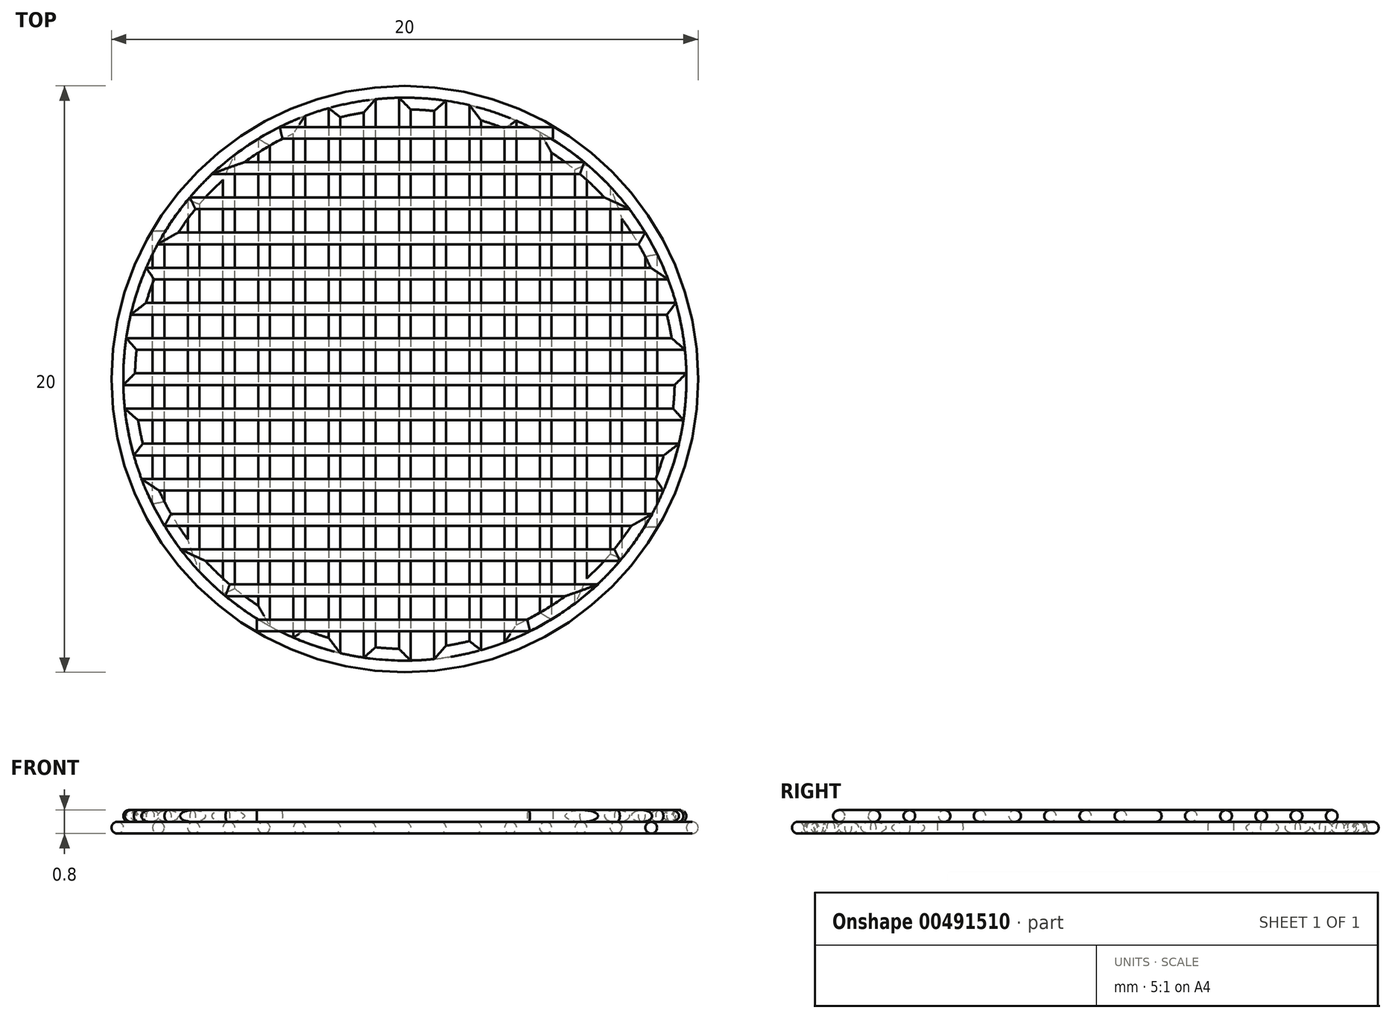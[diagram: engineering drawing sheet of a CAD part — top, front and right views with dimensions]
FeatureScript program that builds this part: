
annotation { "Feature Type Name" : "Feature", "Feature Type Description" : "" }
export const myFeature = defineFeature(function(context is Context, id is Id, definition is map)
    precondition{}
    {
        {
            assignVariable(context, id + "F0", {"name" : "d", "anyValue" : 0.4 * mm});
        }
        {
            var Q0;
            Q0=qCreatedBy(makeId("Top.planeOp"),FACE);
            cPlane(context, id + "F1", {"entities" : qUnion([Q0]), "cplaneType" : CPlaneType.OFFSET, "offset" : getVariable(context, 'd') / 2, "width" : 150 * mm, "height" : 150 * mm});
        }
        {
            var Q0;
            Q0=qCreatedBy(id+"F1.planeOp",FACE);
            var sketch = newSketch(context, id + "F2", { "sketchPlane" : qUnion([Q0])});
            skLineSegment(sketch, "E0.bottom", {"start": v(10, 10) * mm, "end": v(-10, 10) * mm, "construction": true});
            skLineSegment(sketch, "E0.top", {"start": v(10, -10) * mm, "end": v(-10, -10) * mm, "construction": true});
            skLineSegment(sketch, "E0.left", {"start": v(10, 10) * mm, "end": v(10, -10) * mm, "construction": true});
            skLineSegment(sketch, "E0.right", {"start": v(-10, 10) * mm, "end": v(-10, -10) * mm, "construction": true});
            skPoint(sketch, "E0.middle", {"position": v(0, 0) * mm});
            skCircle(sketch, "E1", {"center": v(0, 0) * mm, "radius": 9.8 * mm});
            skCircle(sketch, "E2", {"center": v(0, 0) * mm, "radius": 9.4 * mm, "construction": true});
            skLineSegment(sketch, "E3", {"start": v(10, -10) * mm, "end": v(9.6, -10) * mm, "construction": true});
            skLineSegment(sketch, "E4", {"start": v(9.6, -10) * mm, "end": v(8.4, -10) * mm, "construction": true});
            skLineSegment(sketch, "E5", {"start": v(8.4, -10) * mm, "end": v(7.2, -10) * mm, "construction": true});
            skLineSegment(sketch, "E6", {"start": v(7.2, -10) * mm, "end": v(6, -10) * mm, "construction": true});
            skLineSegment(sketch, "E7", {"start": v(6, -10) * mm, "end": v(4.8, -10) * mm, "construction": true});
            skLineSegment(sketch, "E8", {"start": v(4.8, -10) * mm, "end": v(3.6, -10) * mm, "construction": true});
            skLineSegment(sketch, "E9", {"start": v(3.6, -10) * mm, "end": v(2.4, -10) * mm, "construction": true});
            skLineSegment(sketch, "E10", {"start": v(2.4, -10) * mm, "end": v(1.2, -10) * mm, "construction": true});
            skLineSegment(sketch, "E11", {"start": v(1.2, -10) * mm, "end": v(0, -10) * mm, "construction": true});
            skLineSegment(sketch, "E12", {"start": v(0, -10) * mm, "end": v(-1.2, -10) * mm, "construction": true});
            skLineSegment(sketch, "E13", {"start": v(-1.2, -10) * mm, "end": v(-2.4, -10) * mm, "construction": true});
            skLineSegment(sketch, "E14", {"start": v(-2.4, -10) * mm, "end": v(-3.6, -10) * mm, "construction": true});
            skLineSegment(sketch, "E15", {"start": v(-3.6, -10) * mm, "end": v(-4.8, -10) * mm, "construction": true});
            skLineSegment(sketch, "E16", {"start": v(-4.8, -10) * mm, "end": v(-6, -10) * mm, "construction": true});
            skLineSegment(sketch, "E17", {"start": v(-6, -10) * mm, "end": v(-10, -10) * mm, "construction": true});
            skLineSegment(sketch, "E18", {"start": v(-6, -10) * mm, "end": v(-7.2, -10) * mm, "construction": true});
            skLineSegment(sketch, "E19", {"start": v(-7.2, -10) * mm, "end": v(-8.4, -10) * mm, "construction": true});
            skLineSegment(sketch, "E20", {"start": v(-8.4, -10) * mm, "end": v(-9.6, -10) * mm, "construction": true});
            skLineSegment(sketch, "E21", {"start": v(-9.6, -10) * mm, "end": v(-10, -10) * mm, "construction": true});
            skLineSegment(sketch, "E22", {"start": v(9.6, -10) * mm, "end": v(9.6, 10) * mm, "construction": true});
            skLineSegment(sketch, "E23", {"start": v(9.6, 10) * mm, "end": v(10, 10) * mm, "construction": true});
            skLineSegment(sketch, "E24", {"start": v(-9.6, -10) * mm, "end": v(-9.6, 10) * mm, "construction": true});
            skLineSegment(sketch, "E25", {"start": v(-9.6, 10) * mm, "end": v(-10, 10) * mm, "construction": true});
            skLineSegment(sketch, "E26", {"start": v(7.2, -10) * mm, "end": v(7.2, -6.04) * mm, "construction": true});
            skLineSegment(sketch, "E27", {"start": v(7.2, -6.04) * mm, "end": v(7.2, 6.04) * mm});
            skLineSegment(sketch, "E28", {"start": v(7.2, 6.04) * mm, "end": v(7.2, 10) * mm, "construction": true});
            skLineSegment(sketch, "E29", {"start": v(6, -10) * mm, "end": v(6, -7.24) * mm, "construction": true});
            skLineSegment(sketch, "E30", {"start": v(6, -7.24) * mm, "end": v(6, 7.24) * mm});
            skLineSegment(sketch, "E31", {"start": v(6, 7.24) * mm, "end": v(6, 10) * mm, "construction": true});
            skLineSegment(sketch, "E32", {"start": v(6, 10) * mm, "end": v(7.2, 10) * mm, "construction": true});
            skLineSegment(sketch, "E33", {"start": v(4.8, -10) * mm, "end": v(4.8, -8.08) * mm, "construction": true});
            skLineSegment(sketch, "E34", {"start": v(4.8, -8.08) * mm, "end": v(4.8, 8.08) * mm});
            skLineSegment(sketch, "E35", {"start": v(4.8, 8.08) * mm, "end": v(4.8, 10) * mm, "construction": true});
            skLineSegment(sketch, "E36", {"start": v(4.8, 10) * mm, "end": v(6, 10) * mm, "construction": true});
            skLineSegment(sketch, "E37", {"start": v(3.6, -10) * mm, "end": v(3.6, -8.68) * mm, "construction": true});
            skLineSegment(sketch, "E38", {"start": v(3.6, -8.68) * mm, "end": v(3.6, 8.68) * mm});
            skLineSegment(sketch, "E39", {"start": v(3.6, 8.68) * mm, "end": v(3.6, 10) * mm, "construction": true});
            skLineSegment(sketch, "E40", {"start": v(3.6, 10) * mm, "end": v(4.8, 10) * mm, "construction": true});
            skLineSegment(sketch, "E41", {"start": v(2.4, -10) * mm, "end": v(2.4, -9.09) * mm, "construction": true});
            skLineSegment(sketch, "E42", {"start": v(2.4, -9.09) * mm, "end": v(2.4, 9.09) * mm});
            skLineSegment(sketch, "E43", {"start": v(2.4, 9.09) * mm, "end": v(2.4, 10) * mm, "construction": true});
            skLineSegment(sketch, "E44", {"start": v(2.4, 10) * mm, "end": v(3.6, 10) * mm, "construction": true});
            skLineSegment(sketch, "E45", {"start": v(1.2, -10) * mm, "end": v(1.2, -9.32) * mm, "construction": true});
            skLineSegment(sketch, "E46", {"start": v(1.2, -9.32) * mm, "end": v(1.2, 9.32) * mm});
            skLineSegment(sketch, "E47", {"start": v(1.2, 9.32) * mm, "end": v(1.2, 10) * mm, "construction": true});
            skLineSegment(sketch, "E48", {"start": v(1.2, 10) * mm, "end": v(2.4, 10) * mm, "construction": true});
            skLineSegment(sketch, "E49", {"start": v(0, -10) * mm, "end": v(0, -9.4) * mm, "construction": true});
            skLineSegment(sketch, "E50", {"start": v(0, -9.4) * mm, "end": v(0, 9.4) * mm});
            skLineSegment(sketch, "E51", {"start": v(0, 9.4) * mm, "end": v(0, 10) * mm, "construction": true});
            skLineSegment(sketch, "E52", {"start": v(0, 10) * mm, "end": v(1.2, 10) * mm, "construction": true});
            skLineSegment(sketch, "E53", {"start": v(-1.2, -10) * mm, "end": v(-1.2, -9.32) * mm, "construction": true});
            skLineSegment(sketch, "E54", {"start": v(-1.2, -9.32) * mm, "end": v(-1.2, 9.32) * mm});
            skLineSegment(sketch, "E55", {"start": v(-1.2, 9.32) * mm, "end": v(-1.2, 10) * mm, "construction": true});
            skLineSegment(sketch, "E56", {"start": v(-1.2, 10) * mm, "end": v(0, 10) * mm, "construction": true});
            skLineSegment(sketch, "E57", {"start": v(-2.4, -10) * mm, "end": v(-2.4, -9.09) * mm, "construction": true});
            skLineSegment(sketch, "E58", {"start": v(-2.4, -9.09) * mm, "end": v(-2.4, 9.09) * mm});
            skLineSegment(sketch, "E59", {"start": v(-2.4, 9.09) * mm, "end": v(-2.4, 10) * mm, "construction": true});
            skLineSegment(sketch, "E60", {"start": v(-2.4, 10) * mm, "end": v(-1.2, 10) * mm, "construction": true});
            skLineSegment(sketch, "E61", {"start": v(-3.6, -10) * mm, "end": v(-3.6, -8.68) * mm, "construction": true});
            skLineSegment(sketch, "E62", {"start": v(-3.6, -8.68) * mm, "end": v(-3.6, 8.68) * mm});
            skLineSegment(sketch, "E63", {"start": v(-3.6, 8.68) * mm, "end": v(-3.6, 10) * mm, "construction": true});
            skLineSegment(sketch, "E64", {"start": v(-3.6, 10) * mm, "end": v(-2.4, 10) * mm, "construction": true});
            skLineSegment(sketch, "E65", {"start": v(-4.8, -10) * mm, "end": v(-4.8, -8.08) * mm, "construction": true});
            skLineSegment(sketch, "E66", {"start": v(-4.8, -8.08) * mm, "end": v(-4.8, 8.08) * mm});
            skLineSegment(sketch, "E67", {"start": v(-4.8, 8.08) * mm, "end": v(-4.8, 10) * mm, "construction": true});
            skLineSegment(sketch, "E68", {"start": v(-4.8, 10) * mm, "end": v(-3.6, 10) * mm, "construction": true});
            skLineSegment(sketch, "E69", {"start": v(-6, -10) * mm, "end": v(-6, -7.24) * mm, "construction": true});
            skLineSegment(sketch, "E70", {"start": v(-6, -7.24) * mm, "end": v(-6, 7.24) * mm});
            skLineSegment(sketch, "E71", {"start": v(-6, 7.24) * mm, "end": v(-6, 10) * mm, "construction": true});
            skLineSegment(sketch, "E72", {"start": v(-6, 10) * mm, "end": v(-4.8, 10) * mm, "construction": true});
            skLineSegment(sketch, "E73", {"start": v(-7.2, -10) * mm, "end": v(-7.2, -6.04) * mm, "construction": true});
            skLineSegment(sketch, "E74", {"start": v(-7.2, -6.04) * mm, "end": v(-7.2, 6.04) * mm});
            skLineSegment(sketch, "E75", {"start": v(-7.2, 6.04) * mm, "end": v(-7.2, 10) * mm, "construction": true});
            skLineSegment(sketch, "E76", {"start": v(-7.2, 10) * mm, "end": v(-6, 10) * mm, "construction": true});
            skLineSegment(sketch, "E77", {"start": v(-8.4, -10) * mm, "end": v(-8.4, -4.22) * mm, "construction": true});
            skArc(sketch, "E78", {"start": v(6, 7.24) * mm, "mid": v(5.42, 7.68) * mm, "end": v(4.8, 8.08) * mm});
            skArc(sketch, "E79", {"start": v(3.6, 8.68) * mm, "mid": v(3, 8.9) * mm, "end": v(2.4, 9.09) * mm});
            skArc(sketch, "E80", {"start": v(1.2, 9.32) * mm, "mid": v(0.6, 9.38) * mm, "end": v(0, 9.4) * mm});
            skArc(sketch, "E81", {"start": v(-1.2, 9.32) * mm, "mid": v(-1.8, 9.23) * mm, "end": v(-2.4, 9.09) * mm});
            skArc(sketch, "E82", {"start": v(-3.6, 8.68) * mm, "mid": v(-4.21, 8.4) * mm, "end": v(-4.8, 8.08) * mm});
            skArc(sketch, "E83", {"start": v(-6, 7.24) * mm, "mid": v(-6.63, 6.67) * mm, "end": v(-7.2, 6.04) * mm});
            skArc(sketch, "E84", {"start": v(7.2, -6.04) * mm, "mid": v(6.63, -6.67) * mm, "end": v(6, -7.24) * mm});
            skArc(sketch, "E85", {"start": v(4.8, -8.08) * mm, "mid": v(4.21, -8.4) * mm, "end": v(3.6, -8.68) * mm});
            skArc(sketch, "E86", {"start": v(2.4, -9.09) * mm, "mid": v(1.8, -9.23) * mm, "end": v(1.2, -9.32) * mm});
            skArc(sketch, "E87", {"start": v(0, -9.4) * mm, "mid": v(-0.6, -9.38) * mm, "end": v(-1.2, -9.32) * mm});
            skArc(sketch, "E88", {"start": v(-2.4, -9.09) * mm, "mid": v(-3, -8.9) * mm, "end": v(-3.6, -8.68) * mm});
            skArc(sketch, "E89", {"start": v(-4.8, -8.08) * mm, "mid": v(-5.42, -7.68) * mm, "end": v(-6, -7.24) * mm});
            skArc(sketch, "E90", {"start": v(-7.2, -6.04) * mm, "mid": v(-7.85, -5.17) * mm, "end": v(-8.4, -4.22) * mm});
            skLineSegment(sketch, "E91", {"start": v(8.4, -10) * mm, "end": v(8.4, -5.05) * mm, "construction": true});
            skLineSegment(sketch, "E92", {"start": v(8.4, -5.05) * mm, "end": v(8.4, 4.22) * mm});
            skLineSegment(sketch, "E93", {"start": v(8.4, 4.22) * mm, "end": v(8.4, 10) * mm, "construction": true});
            skLineSegment(sketch, "E94", {"start": v(8.4, 10) * mm, "end": v(9.6, 10) * mm, "construction": true});
            skLineSegment(sketch, "E95", {"start": v(7.2, 10) * mm, "end": v(8.4, 10) * mm, "construction": true});
            skLineSegment(sketch, "E96", {"start": v(-8.4, -4.22) * mm, "end": v(-8.4, 5.05) * mm});
            skLineSegment(sketch, "E97", {"start": v(-8.4, 5.05) * mm, "end": v(-8.4, 10) * mm, "construction": true});
            skLineSegment(sketch, "E98", {"start": v(-8.4, 10) * mm, "end": v(-7.2, 10) * mm, "construction": true});
            skLineSegment(sketch, "E99", {"start": v(-8.4, 10) * mm, "end": v(-9.6, 10) * mm, "construction": true});
            skArc(sketch, "E100", {"start": v(8.4, 4.22) * mm, "mid": v(7.85, 5.17) * mm, "end": v(7.2, 6.04) * mm});
            skLineSegment(sketch, "E101", {"start": v(-8.4, -4.22) * mm, "end": v(-8.4, 4.22) * mm});
            skLineSegment(sketch, "E102", {"start": v(8.4, -4.22) * mm, "end": v(8.4, 4.22) * mm});
            skArc(sketch, "E103", {"start": v(-8.4, 4.22) * mm, "mid": v(-9.15, 2.17) * mm, "end": v(-9.4, 0) * mm});
            skArc(sketch, "E104", {"start": v(8.4, -4.22) * mm, "mid": v(9.15, -2.17) * mm, "end": v(9.4, 0) * mm});
            skSolve(sketch);
        }
        {
            var Q0;
            Q0=sQuery(id+"F2.wireOp",EDGE,"E92");
            var Q1;
            Q1=sQuery(id+"F2.wireOp",VERTEX,"E91.end");
            cPlane(context, id + "F3", {"entities" : qUnion([Q0, Q1]), "cplaneType" : CPlaneType.LINE_POINT, "offset" : 25 * mm, "width" : 150 * mm, "height" : 150 * mm});
        }
        {
            var Q0;
            Q0=qCreatedBy(id+"F3.planeOp",FACE);
            var sketch = newSketch(context, id + "F4", { "sketchPlane" : qUnion([Q0])});
            skCircle(sketch, "E105", {"center": v(-8.4, 0.2) * mm, "radius": 0.2 * mm});
            skSolve(sketch);
        }
        {
            var Q0;
            Q0=makeQuery(id+"F4.imprint","IMPRINT",FACE,{"disambiguationData":[TD([[makeQuery(id+"F4.imprint","IMPRINT",EDGE,{"derivedFrom":sQuery(id+"F4.wireOp",EDGE,"E105")}),1.0]])]});
            var Q1;
            Q1=sQuery(id+"F2.wireOp",EDGE,"E100");
            var Q2;
            Q2=sQuery(id+"F2.wireOp",EDGE,"E27");
            var Q3;
            Q3=sQuery(id+"F2.wireOp",EDGE,"E84");
            var Q4;
            Q4=sQuery(id+"F2.wireOp",EDGE,"E30");
            var Q5;
            Q5=sQuery(id+"F2.wireOp",EDGE,"E78");
            var Q6;
            Q6=sQuery(id+"F2.wireOp",EDGE,"E34");
            var Q7;
            Q7=sQuery(id+"F2.wireOp",EDGE,"E85");
            var Q8;
            Q8=sQuery(id+"F2.wireOp",EDGE,"E38");
            var Q9;
            Q9=sQuery(id+"F2.wireOp",EDGE,"E79");
            var Q10;
            Q10=sQuery(id+"F2.wireOp",EDGE,"E42");
            var Q11;
            Q11=sQuery(id+"F2.wireOp",EDGE,"E86");
            var Q12;
            Q12=sQuery(id+"F2.wireOp",EDGE,"E46");
            var Q13;
            Q13=sQuery(id+"F2.wireOp",EDGE,"E50");
            var Q14;
            Q14=sQuery(id+"F2.wireOp",EDGE,"E87");
            var Q15;
            Q15=sQuery(id+"F2.wireOp",EDGE,"E80");
            var Q16;
            Q16=sQuery(id+"F2.wireOp",EDGE,"E81");
            var Q17;
            Q17=sQuery(id+"F2.wireOp",EDGE,"E54");
            var Q18;
            Q18=sQuery(id+"F2.wireOp",EDGE,"E58");
            var Q19;
            Q19=sQuery(id+"F2.wireOp",EDGE,"E88");
            var Q20;
            Q20=sQuery(id+"F2.wireOp",EDGE,"E62");
            var Q21;
            Q21=sQuery(id+"F2.wireOp",EDGE,"E66");
            var Q22;
            Q22=sQuery(id+"F2.wireOp",EDGE,"E82");
            var Q23;
            Q23=sQuery(id+"F2.wireOp",EDGE,"E89");
            var Q24;
            Q24=sQuery(id+"F2.wireOp",EDGE,"E70");
            var Q25;
            Q25=sQuery(id+"F2.wireOp",EDGE,"E83");
            var Q26;
            Q26=sQuery(id+"F2.wireOp",EDGE,"E74");
            var Q27;
            Q27=sQuery(id+"F2.wireOp",EDGE,"E90");
            var Q28;
            Q28=sQuery(id+"F2.wireOp",EDGE,"E92");
            var Q29;
            Q29=sQuery(id+"F2.wireOp",EDGE,"E96");
            sweep(context, id + "F5", {"profiles" : qUnion([Q0]), "path" : qUnion([Q1, Q2, Q3, Q4, Q5, Q6, Q7, Q8, Q9, Q10, Q11, Q12, Q13, Q14, Q15, Q16, Q17, Q18, Q19, Q20, Q21, Q22, Q23, Q24, Q25, Q26, Q27, Q28, Q29])});
        }
        {
            var Q0;
            Q0=qCreatedBy(makeId("Front.planeOp"),FACE);
            var sketch = newSketch(context, id + "F6", { "sketchPlane" : qUnion([Q0])});
            skCircle(sketch, "E106", {"center": v(9.8, 0.2) * mm, "radius": 0.2 * mm});
            skSolve(sketch);
        }
        {
            var Q0;
            Q0 = qSketchRegion(id + "F6", true);
            var Q1;
            Q1=sQuery(id+"F2.wireOp",EDGE,"E1");
            sweep(context, id + "F7", {"profiles" : qUnion([Q0]), "path" : qUnion([Q1])});
        }
        {
            var Q0;
            Q0=qCreatedBy(id+"F1.planeOp",FACE);
            cPlane(context, id + "F8", {"entities" : qUnion([Q0]), "cplaneType" : CPlaneType.OFFSET, "offset" : getVariable(context, 'd'), "width" : 150 * mm, "height" : 150 * mm});
        }
        {
            var Q0;
            Q0=qCreatedBy(id+"F8.planeOp",FACE);
            var sketch = newSketch(context, id + "F9", { "sketchPlane" : qUnion([Q0])});
            skLineSegment(sketch, "E107.bottom", {"start": v(-10, 10) * mm, "end": v(-10, -10) * mm, "construction": true});
            skLineSegment(sketch, "E107.top", {"start": v(10, 10) * mm, "end": v(10, -10) * mm, "construction": true});
            skLineSegment(sketch, "E107.left", {"start": v(-10, 10) * mm, "end": v(10, 10) * mm, "construction": true});
            skLineSegment(sketch, "E107.right", {"start": v(-10, -10) * mm, "end": v(10, -10) * mm, "construction": true});
            skPoint(sketch, "E107.middle", {"position": v(0, 0) * mm});
            skCircle(sketch, "E108", {"center": v(0, 0) * mm, "radius": 9.8 * mm});
            skCircle(sketch, "E109", {"center": v(0, 0) * mm, "radius": 9.4 * mm, "construction": true});
            skLineSegment(sketch, "E110", {"start": v(10, 10) * mm, "end": v(10, 9.6) * mm, "construction": true});
            skLineSegment(sketch, "E111", {"start": v(10, 9.6) * mm, "end": v(10, 8.4) * mm, "construction": true});
            skLineSegment(sketch, "E112", {"start": v(10, 8.4) * mm, "end": v(10, 7.2) * mm, "construction": true});
            skLineSegment(sketch, "E113", {"start": v(10, 7.2) * mm, "end": v(10, 6) * mm, "construction": true});
            skLineSegment(sketch, "E114", {"start": v(10, 6) * mm, "end": v(10, 4.8) * mm, "construction": true});
            skLineSegment(sketch, "E115", {"start": v(10, 4.8) * mm, "end": v(10, 3.6) * mm, "construction": true});
            skLineSegment(sketch, "E116", {"start": v(10, 3.6) * mm, "end": v(10, 2.4) * mm, "construction": true});
            skLineSegment(sketch, "E117", {"start": v(10, 2.4) * mm, "end": v(10, 1.2) * mm, "construction": true});
            skLineSegment(sketch, "E118", {"start": v(10, 1.2) * mm, "end": v(10, 0) * mm, "construction": true});
            skLineSegment(sketch, "E119", {"start": v(10, 0) * mm, "end": v(10, -1.2) * mm, "construction": true});
            skLineSegment(sketch, "E120", {"start": v(10, -1.2) * mm, "end": v(10, -2.4) * mm, "construction": true});
            skLineSegment(sketch, "E121", {"start": v(10, -2.4) * mm, "end": v(10, -3.6) * mm, "construction": true});
            skLineSegment(sketch, "E122", {"start": v(10, -3.6) * mm, "end": v(10, -4.8) * mm, "construction": true});
            skLineSegment(sketch, "E123", {"start": v(10, -4.8) * mm, "end": v(10, -6) * mm, "construction": true});
            skLineSegment(sketch, "E124", {"start": v(10, -6) * mm, "end": v(10, -10) * mm, "construction": true});
            skLineSegment(sketch, "E125", {"start": v(10, -6) * mm, "end": v(10, -7.2) * mm, "construction": true});
            skLineSegment(sketch, "E126", {"start": v(10, -7.2) * mm, "end": v(10, -8.4) * mm, "construction": true});
            skLineSegment(sketch, "E127", {"start": v(10, -8.4) * mm, "end": v(10, -9.6) * mm, "construction": true});
            skLineSegment(sketch, "E128", {"start": v(10, -9.6) * mm, "end": v(10, -10) * mm, "construction": true});
            skLineSegment(sketch, "E129", {"start": v(10, 9.6) * mm, "end": v(-10, 9.6) * mm, "construction": true});
            skLineSegment(sketch, "E130", {"start": v(-10, 9.6) * mm, "end": v(-10, 10) * mm, "construction": true});
            skLineSegment(sketch, "E131", {"start": v(10, -9.6) * mm, "end": v(-10, -9.6) * mm, "construction": true});
            skLineSegment(sketch, "E132", {"start": v(-10, -9.6) * mm, "end": v(-10, -10) * mm, "construction": true});
            skLineSegment(sketch, "E133", {"start": v(10, 7.2) * mm, "end": v(6.04, 7.2) * mm, "construction": true});
            skLineSegment(sketch, "E134", {"start": v(6.04, 7.2) * mm, "end": v(-6.04, 7.2) * mm});
            skLineSegment(sketch, "E135", {"start": v(-6.04, 7.2) * mm, "end": v(-10, 7.2) * mm, "construction": true});
            skLineSegment(sketch, "E136", {"start": v(10, 6) * mm, "end": v(7.24, 6) * mm, "construction": true});
            skLineSegment(sketch, "E137", {"start": v(7.24, 6) * mm, "end": v(-7.24, 6) * mm});
            skLineSegment(sketch, "E138", {"start": v(-7.24, 6) * mm, "end": v(-10, 6) * mm, "construction": true});
            skLineSegment(sketch, "E139", {"start": v(-10, 6) * mm, "end": v(-10, 7.2) * mm, "construction": true});
            skLineSegment(sketch, "E140", {"start": v(10, 4.8) * mm, "end": v(8.08, 4.8) * mm, "construction": true});
            skLineSegment(sketch, "E141", {"start": v(8.08, 4.8) * mm, "end": v(-8.08, 4.8) * mm});
            skLineSegment(sketch, "E142", {"start": v(-8.08, 4.8) * mm, "end": v(-10, 4.8) * mm, "construction": true});
            skLineSegment(sketch, "E143", {"start": v(-10, 4.8) * mm, "end": v(-10, 6) * mm, "construction": true});
            skLineSegment(sketch, "E144", {"start": v(10, 3.6) * mm, "end": v(8.68, 3.6) * mm, "construction": true});
            skLineSegment(sketch, "E145", {"start": v(8.68, 3.6) * mm, "end": v(-8.68, 3.6) * mm});
            skLineSegment(sketch, "E146", {"start": v(-8.68, 3.6) * mm, "end": v(-10, 3.6) * mm, "construction": true});
            skLineSegment(sketch, "E147", {"start": v(-10, 3.6) * mm, "end": v(-10, 4.8) * mm, "construction": true});
            skLineSegment(sketch, "E148", {"start": v(10, 2.4) * mm, "end": v(9.09, 2.4) * mm, "construction": true});
            skLineSegment(sketch, "E149", {"start": v(9.09, 2.4) * mm, "end": v(-9.09, 2.4) * mm});
            skLineSegment(sketch, "E150", {"start": v(-9.09, 2.4) * mm, "end": v(-10, 2.4) * mm, "construction": true});
            skLineSegment(sketch, "E151", {"start": v(-10, 2.4) * mm, "end": v(-10, 3.6) * mm, "construction": true});
            skLineSegment(sketch, "E152", {"start": v(10, 1.2) * mm, "end": v(9.32, 1.2) * mm, "construction": true});
            skLineSegment(sketch, "E153", {"start": v(9.32, 1.2) * mm, "end": v(-9.32, 1.2) * mm});
            skLineSegment(sketch, "E154", {"start": v(-9.32, 1.2) * mm, "end": v(-10, 1.2) * mm, "construction": true});
            skLineSegment(sketch, "E155", {"start": v(-10, 1.2) * mm, "end": v(-10, 2.4) * mm, "construction": true});
            skLineSegment(sketch, "E156", {"start": v(10, 0) * mm, "end": v(9.4, 0) * mm, "construction": true});
            skLineSegment(sketch, "E157", {"start": v(9.4, 0) * mm, "end": v(-9.4, 0) * mm});
            skLineSegment(sketch, "E158", {"start": v(-9.4, 0) * mm, "end": v(-10, 0) * mm, "construction": true});
            skLineSegment(sketch, "E159", {"start": v(-10, 0) * mm, "end": v(-10, 1.2) * mm, "construction": true});
            skLineSegment(sketch, "E160", {"start": v(10, -1.2) * mm, "end": v(9.32, -1.2) * mm, "construction": true});
            skLineSegment(sketch, "E161", {"start": v(9.32, -1.2) * mm, "end": v(-9.32, -1.2) * mm});
            skLineSegment(sketch, "E162", {"start": v(-9.32, -1.2) * mm, "end": v(-10, -1.2) * mm, "construction": true});
            skLineSegment(sketch, "E163", {"start": v(-10, -1.2) * mm, "end": v(-10, 0) * mm, "construction": true});
            skLineSegment(sketch, "E164", {"start": v(10, -2.4) * mm, "end": v(9.09, -2.4) * mm, "construction": true});
            skLineSegment(sketch, "E165", {"start": v(9.09, -2.4) * mm, "end": v(-9.09, -2.4) * mm});
            skLineSegment(sketch, "E166", {"start": v(-9.09, -2.4) * mm, "end": v(-10, -2.4) * mm, "construction": true});
            skLineSegment(sketch, "E167", {"start": v(-10, -2.4) * mm, "end": v(-10, -1.2) * mm, "construction": true});
            skLineSegment(sketch, "E168", {"start": v(10, -3.6) * mm, "end": v(8.68, -3.6) * mm, "construction": true});
            skLineSegment(sketch, "E169", {"start": v(8.68, -3.6) * mm, "end": v(-8.68, -3.6) * mm});
            skLineSegment(sketch, "E170", {"start": v(-8.68, -3.6) * mm, "end": v(-10, -3.6) * mm, "construction": true});
            skLineSegment(sketch, "E171", {"start": v(-10, -3.6) * mm, "end": v(-10, -2.4) * mm, "construction": true});
            skLineSegment(sketch, "E172", {"start": v(10, -4.8) * mm, "end": v(8.08, -4.8) * mm, "construction": true});
            skLineSegment(sketch, "E173", {"start": v(8.08, -4.8) * mm, "end": v(-8.08, -4.8) * mm});
            skLineSegment(sketch, "E174", {"start": v(-8.08, -4.8) * mm, "end": v(-10, -4.8) * mm, "construction": true});
            skLineSegment(sketch, "E175", {"start": v(-10, -4.8) * mm, "end": v(-10, -3.6) * mm, "construction": true});
            skLineSegment(sketch, "E176", {"start": v(10, -6) * mm, "end": v(7.24, -6) * mm, "construction": true});
            skLineSegment(sketch, "E177", {"start": v(7.24, -6) * mm, "end": v(-7.24, -6) * mm});
            skLineSegment(sketch, "E178", {"start": v(-7.24, -6) * mm, "end": v(-10, -6) * mm, "construction": true});
            skLineSegment(sketch, "E179", {"start": v(-10, -6) * mm, "end": v(-10, -4.8) * mm, "construction": true});
            skLineSegment(sketch, "E180", {"start": v(10, -7.2) * mm, "end": v(6.04, -7.2) * mm, "construction": true});
            skLineSegment(sketch, "E181", {"start": v(6.04, -7.2) * mm, "end": v(-6.04, -7.2) * mm});
            skLineSegment(sketch, "E182", {"start": v(-6.04, -7.2) * mm, "end": v(-10, -7.2) * mm, "construction": true});
            skLineSegment(sketch, "E183", {"start": v(-10, -7.2) * mm, "end": v(-10, -6) * mm, "construction": true});
            skLineSegment(sketch, "E184", {"start": v(10, -8.4) * mm, "end": v(4.22, -8.4) * mm, "construction": true});
            skArc(sketch, "E185", {"start": v(-7.24, 6) * mm, "mid": v(-7.68, 5.42) * mm, "end": v(-8.08, 4.8) * mm});
            skArc(sketch, "E186", {"start": v(-8.68, 3.6) * mm, "mid": v(-8.9, 3) * mm, "end": v(-9.09, 2.4) * mm});
            skArc(sketch, "E187", {"start": v(-9.32, 1.2) * mm, "mid": v(-9.38, 0.6) * mm, "end": v(-9.4, 0) * mm});
            skArc(sketch, "E188", {"start": v(-9.32, -1.2) * mm, "mid": v(-9.23, -1.8) * mm, "end": v(-9.09, -2.4) * mm});
            skArc(sketch, "E189", {"start": v(-8.68, -3.6) * mm, "mid": v(-8.4, -4.21) * mm, "end": v(-8.08, -4.8) * mm});
            skArc(sketch, "E190", {"start": v(-7.24, -6) * mm, "mid": v(-6.67, -6.63) * mm, "end": v(-6.04, -7.2) * mm});
            skArc(sketch, "E191", {"start": v(6.04, 7.2) * mm, "mid": v(6.67, 6.63) * mm, "end": v(7.24, 6) * mm});
            skArc(sketch, "E192", {"start": v(8.08, 4.8) * mm, "mid": v(8.4, 4.21) * mm, "end": v(8.68, 3.6) * mm});
            skArc(sketch, "E193", {"start": v(9.09, 2.4) * mm, "mid": v(9.23, 1.8) * mm, "end": v(9.32, 1.2) * mm});
            skArc(sketch, "E194", {"start": v(9.4, 0) * mm, "mid": v(9.38, -0.6) * mm, "end": v(9.32, -1.2) * mm});
            skArc(sketch, "E195", {"start": v(9.09, -2.4) * mm, "mid": v(8.9, -3) * mm, "end": v(8.68, -3.6) * mm});
            skArc(sketch, "E196", {"start": v(8.08, -4.8) * mm, "mid": v(7.68, -5.42) * mm, "end": v(7.24, -6) * mm});
            skArc(sketch, "E197", {"start": v(6.04, -7.2) * mm, "mid": v(5.17, -7.85) * mm, "end": v(4.22, -8.4) * mm});
            skLineSegment(sketch, "E198", {"start": v(10, 8.4) * mm, "end": v(5.05, 8.4) * mm, "construction": true});
            skLineSegment(sketch, "E199", {"start": v(5.05, 8.4) * mm, "end": v(-4.22, 8.4) * mm});
            skLineSegment(sketch, "E200", {"start": v(-4.22, 8.4) * mm, "end": v(-10, 8.4) * mm, "construction": true});
            skLineSegment(sketch, "E201", {"start": v(-10, 8.4) * mm, "end": v(-10, 9.6) * mm, "construction": true});
            skLineSegment(sketch, "E202", {"start": v(-10, 7.2) * mm, "end": v(-10, 8.4) * mm, "construction": true});
            skLineSegment(sketch, "E203", {"start": v(4.22, -8.4) * mm, "end": v(-5.05, -8.4) * mm});
            skLineSegment(sketch, "E204", {"start": v(-5.05, -8.4) * mm, "end": v(-10, -8.4) * mm, "construction": true});
            skLineSegment(sketch, "E205", {"start": v(-10, -8.4) * mm, "end": v(-10, -7.2) * mm, "construction": true});
            skLineSegment(sketch, "E206", {"start": v(-10, -8.4) * mm, "end": v(-10, -9.6) * mm, "construction": true});
            skArc(sketch, "E207", {"start": v(-4.22, 8.4) * mm, "mid": v(-5.17, 7.85) * mm, "end": v(-6.04, 7.2) * mm});
            skLineSegment(sketch, "E208", {"start": v(4.22, -8.4) * mm, "end": v(-4.22, -8.4) * mm});
            skLineSegment(sketch, "E209", {"start": v(4.22, 8.4) * mm, "end": v(-4.22, 8.4) * mm});
            skArc(sketch, "E210", {"start": v(-4.22, -8.4) * mm, "mid": v(-2.17, -9.15) * mm, "end": v(0, -9.4) * mm});
            skArc(sketch, "E211", {"start": v(4.22, 8.4) * mm, "mid": v(2.17, 9.15) * mm, "end": v(0, 9.4) * mm});
            skSolve(sketch);
        }
        {
            var Q0;
            Q0=sQuery(id+"F9.wireOp",VERTEX,"E199.start");
            var Q1;
            Q1=sQuery(id+"F9.wireOp",EDGE,"E199");
            cPlane(context, id + "F10", {"entities" : qUnion([Q0, Q1]), "cplaneType" : CPlaneType.LINE_POINT, "offset" : 25 * mm, "width" : 150 * mm, "height" : 150 * mm});
        }
        {
            var Q0;
            Q0=qCreatedBy(id+"F10.planeOp",FACE);
            var sketch = newSketch(context, id + "F11", { "sketchPlane" : qUnion([Q0])});
            skCircle(sketch, "E212", {"center": v(-8.4, 0.6) * mm, "radius": 0.2 * mm});
            skSolve(sketch);
        }
        {
            var Q0;
            Q0=makeQuery(id+"F11.imprint","IMPRINT",FACE,{"disambiguationData":[TD([[makeQuery(id+"F11.imprint","IMPRINT",EDGE,{"derivedFrom":sQuery(id+"F11.wireOp",EDGE,"E212")}),1.0]])]});
            var Q1;
            Q1=sQuery(id+"F9.wireOp",EDGE,"E199");
            var Q2;
            Q2=sQuery(id+"F9.wireOp",EDGE,"E207");
            var Q3;
            Q3=sQuery(id+"F9.wireOp",EDGE,"E134");
            var Q4;
            Q4=sQuery(id+"F9.wireOp",EDGE,"E191");
            var Q5;
            Q5=sQuery(id+"F9.wireOp",EDGE,"E137");
            var Q6;
            Q6=sQuery(id+"F9.wireOp",EDGE,"E141");
            var Q7;
            Q7=sQuery(id+"F9.wireOp",EDGE,"E192");
            var Q8;
            Q8=sQuery(id+"F9.wireOp",EDGE,"E145");
            var Q9;
            Q9=sQuery(id+"F9.wireOp",EDGE,"E185");
            var Q10;
            Q10=sQuery(id+"F9.wireOp",EDGE,"E149");
            var Q11;
            Q11=sQuery(id+"F9.wireOp",EDGE,"E153");
            var Q12;
            Q12=sQuery(id+"F9.wireOp",EDGE,"E157");
            var Q13;
            Q13=sQuery(id+"F9.wireOp",EDGE,"E161");
            var Q14;
            Q14=sQuery(id+"F9.wireOp",EDGE,"E165");
            var Q15;
            Q15=sQuery(id+"F9.wireOp",EDGE,"E169");
            var Q16;
            Q16=sQuery(id+"F9.wireOp",EDGE,"E173");
            var Q17;
            Q17=sQuery(id+"F9.wireOp",EDGE,"E177");
            var Q18;
            Q18=sQuery(id+"F9.wireOp",EDGE,"E181");
            var Q19;
            Q19=sQuery(id+"F9.wireOp",EDGE,"E203");
            var Q20;
            Q20=sQuery(id+"F9.wireOp",EDGE,"E197");
            var Q21;
            Q21=sQuery(id+"F9.wireOp",EDGE,"E196");
            var Q22;
            Q22=sQuery(id+"F9.wireOp",EDGE,"E195");
            var Q23;
            Q23=sQuery(id+"F9.wireOp",EDGE,"E194");
            var Q24;
            Q24=sQuery(id+"F9.wireOp",EDGE,"E193");
            var Q25;
            Q25=sQuery(id+"F9.wireOp",EDGE,"E190");
            var Q26;
            Q26=sQuery(id+"F9.wireOp",EDGE,"E189");
            var Q27;
            Q27=sQuery(id+"F9.wireOp",EDGE,"E188");
            var Q28;
            Q28=sQuery(id+"F9.wireOp",EDGE,"E187");
            var Q29;
            Q29=sQuery(id+"F9.wireOp",EDGE,"E186");
            sweep(context, id + "F12", {"profiles" : qUnion([Q0]), "path" : qUnion([Q1, Q2, Q3, Q4, Q5, Q6, Q7, Q8, Q9, Q10, Q11, Q12, Q13, Q14, Q15, Q16, Q17, Q18, Q19, Q20, Q21, Q22, Q23, Q24, Q25, Q26, Q27, Q28, Q29])});
        }
    });
